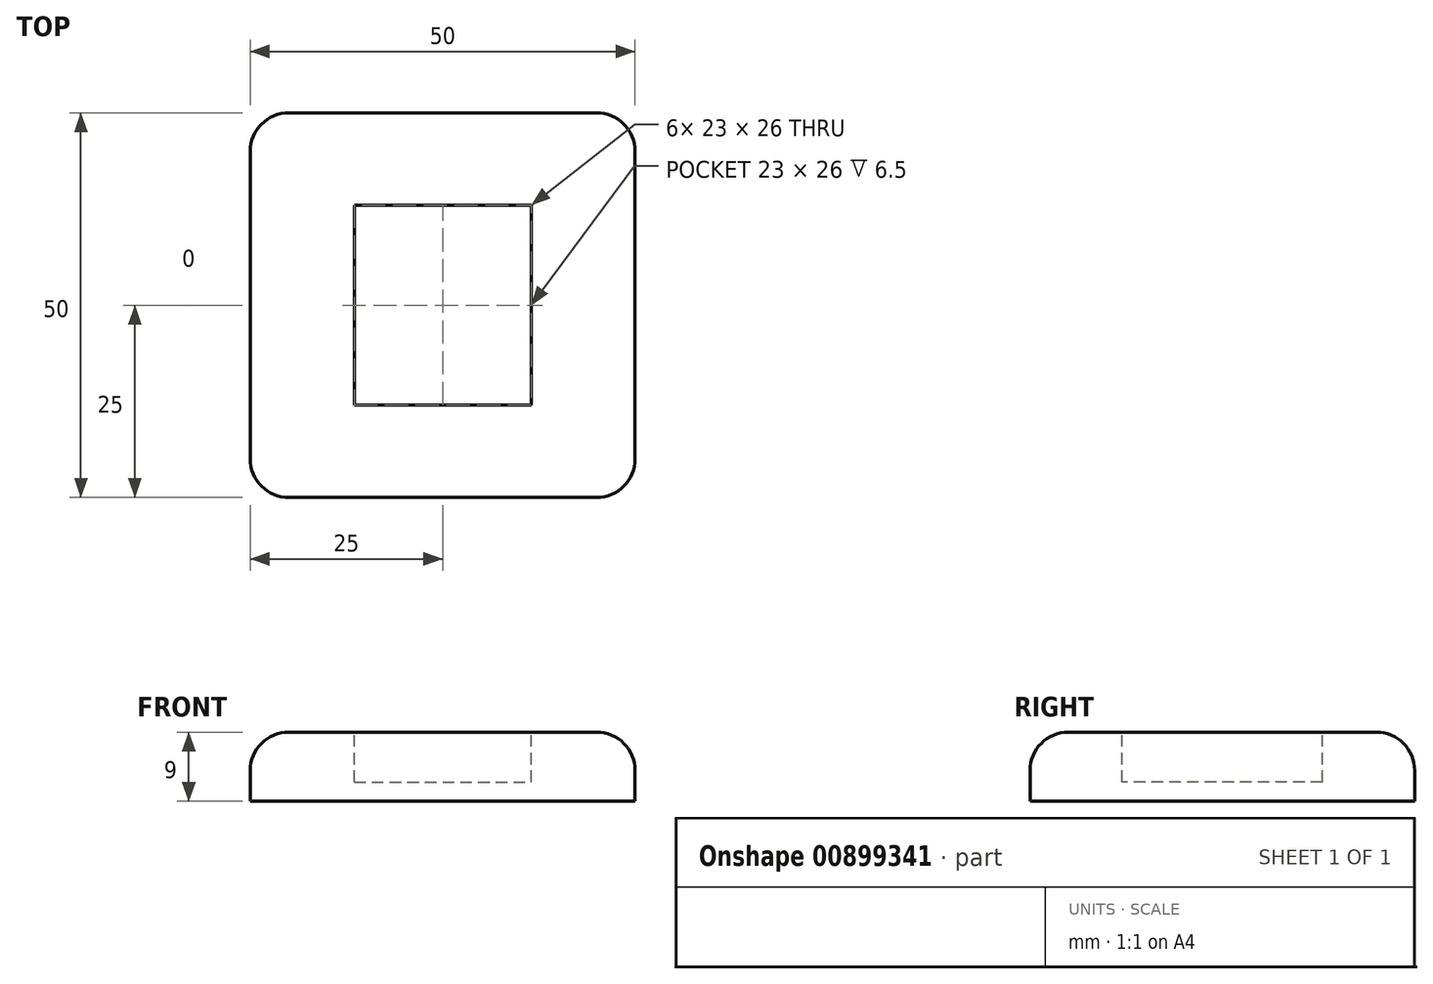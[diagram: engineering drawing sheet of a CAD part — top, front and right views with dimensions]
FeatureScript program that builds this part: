
annotation { "Feature Type Name" : "Feature", "Feature Type Description" : "" }
export const myFeature = defineFeature(function(context is Context, id is Id, definition is map)
    precondition{}
    {
        {
            var Q0;
            Q0=qCreatedBy(makeId("Top.planeOp"),FACE);
            var sketch = newSketch(context, id + "F0", { "sketchPlane" : qUnion([Q0])});
            skLineSegment(sketch, "E0.bottom", {"start": v(-25, 25) * mm, "end": v(25, 25) * mm});
            skLineSegment(sketch, "E0.top", {"start": v(-25, -25) * mm, "end": v(25, -25) * mm});
            skLineSegment(sketch, "E0.left", {"start": v(-25, 25) * mm, "end": v(-25, -25) * mm});
            skLineSegment(sketch, "E0.right", {"start": v(25, 25) * mm, "end": v(25, -25) * mm});
            skSolve(sketch);
        }
        {
            var Q0;
            Q0=makeQuery(id+"F0.imprint","IMPRINT",FACE,{"disambiguationData":[TD([[makeQuery(id+"F0.imprint","IMPRINT",EDGE,{"derivedFrom":sQuery(id+"F0.wireOp",EDGE,"E0.bottom")}),-1.0]])]});
            extrude(context, id + "F1", {"entities" : qUnion([Q0]), "depth" : 9 * mm, "offsetDistance" : 25 * mm});
        }
        {
            var Q0;
            Q0=makeQuery(id+"F1.opExtrude","CAP_FACE",FACE,{"disambiguationData":[OSD([sQuery(id+"F0.wireOp",EDGE,"E0.bottom"),sQuery(id+"F0.wireOp",EDGE,"E0.top"),sQuery(id+"F0.wireOp",EDGE,"E0.left"),sQuery(id+"F0.wireOp",EDGE,"E0.right")])],"isStart":false});
            var sketch = newSketch(context, id + "F2", { "sketchPlane" : qUnion([Q0])});
            skLineSegment(sketch, "E1.bottom", {"start": v(-11.5, 13) * mm, "end": v(11.5, 13) * mm});
            skLineSegment(sketch, "E1.top", {"start": v(-11.5, -13) * mm, "end": v(11.5, -13) * mm});
            skLineSegment(sketch, "E1.left", {"start": v(-11.5, 13) * mm, "end": v(-11.5, -13) * mm});
            skLineSegment(sketch, "E1.right", {"start": v(11.5, 13) * mm, "end": v(11.5, -13) * mm});
            skSolve(sketch);
        }
        {
            var Q0;
            Q0=makeQuery(id+"F2.imprint","IMPRINT",FACE,{"disambiguationData":[TD([[makeQuery(id+"F2.imprint","IMPRINT",EDGE,{"derivedFrom":sQuery(id+"F2.wireOp",EDGE,"E1.bottom")}),-1.0]])]});
            extrude(context, id + "F3", {"entities" : qUnion([Q0]), "operationType" : NewBodyOperationType.REMOVE, "oppositeDirection" : true, "depth" : 6.5 * mm, "offsetDistance" : 25 * mm});
        }
        {
            var Q0;
            Q0=makeQuery(id+"F1.opExtrude","SWEPT_EDGE",EDGE,{"disambiguationData":[OSD([sQuery(id+"F0.wireOp",EDGE,"E0.top"),sQuery(id+"F0.wireOp",EDGE,"E0.left")])]});
            var Q1;
            Q1=makeQuery(id+"F1.opExtrude","SWEPT_EDGE",EDGE,{"disambiguationData":[OSD([sQuery(id+"F0.wireOp",EDGE,"E0.top"),sQuery(id+"F0.wireOp",EDGE,"E0.right")])]});
            var Q2;
            Q2=makeQuery(id+"F1.opExtrude","CAP_EDGE",EDGE,{"disambiguationData":[OSD([sQuery(id+"F0.wireOp",EDGE,"E0.bottom")])],"isStart":false});
            var Q3;
            Q3=makeQuery(id+"F1.opExtrude","CAP_EDGE",EDGE,{"disambiguationData":[OSD([sQuery(id+"F0.wireOp",EDGE,"E0.left")])],"isStart":false});
            var Q4;
            Q4=makeQuery(id+"F1.opExtrude","CAP_EDGE",EDGE,{"disambiguationData":[OSD([sQuery(id+"F0.wireOp",EDGE,"E0.right")])],"isStart":false});
            var Q5;
            Q5=makeQuery(id+"F1.opExtrude","CAP_EDGE",EDGE,{"disambiguationData":[OSD([sQuery(id+"F0.wireOp",EDGE,"E0.top")])],"isStart":false});
            var Q6;
            Q6=makeQuery(id+"F1.opExtrude","SWEPT_EDGE",EDGE,{"disambiguationData":[OSD([sQuery(id+"F0.wireOp",EDGE,"E0.bottom"),sQuery(id+"F0.wireOp",EDGE,"E0.left")])]});
            var Q7;
            Q7=makeQuery(id+"F1.opExtrude","SWEPT_EDGE",EDGE,{"disambiguationData":[OSD([sQuery(id+"F0.wireOp",EDGE,"E0.bottom"),sQuery(id+"F0.wireOp",EDGE,"E0.right")])]});
            fillet(context, id + "F4", {"entities" : qUnion([Q0, Q1, Q2, Q3, Q4, Q5, Q6, Q7]), "radius" : 5 * mm, "allowEdgeOverflow" : false});
        }
    });
